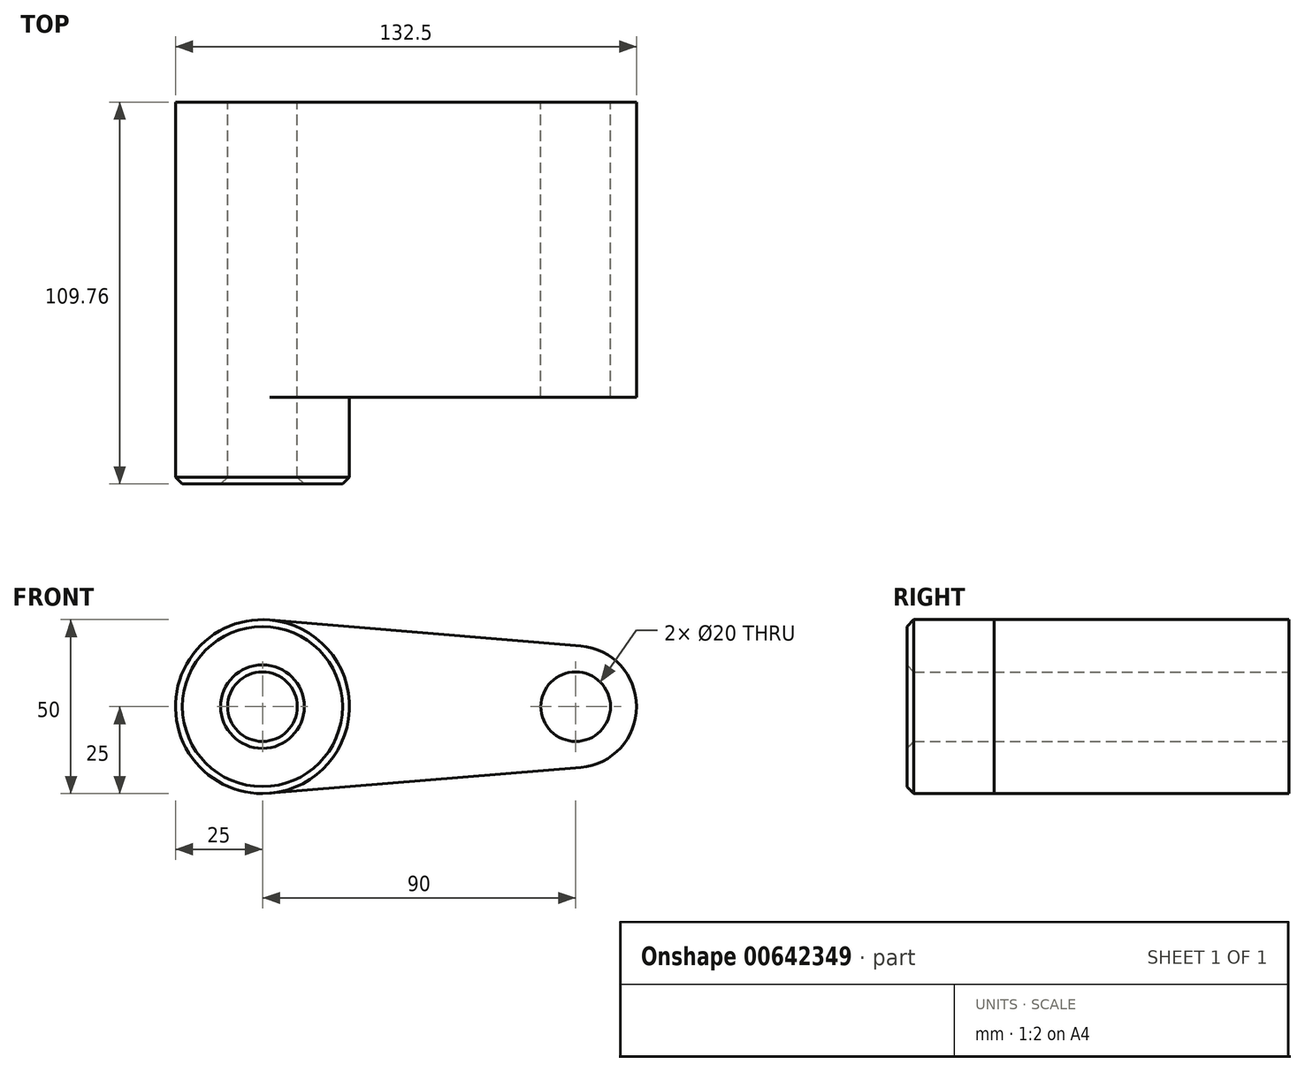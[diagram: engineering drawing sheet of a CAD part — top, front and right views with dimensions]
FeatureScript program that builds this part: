
annotation { "Feature Type Name" : "Feature", "Feature Type Description" : "" }
export const myFeature = defineFeature(function(context is Context, id is Id, definition is map)
    precondition{}
    {
        {
            var Q0;
            Q0=qCreatedBy(makeId("Front.planeOp"),FACE);
            var sketch = newSketch(context, id + "F0", { "sketchPlane" : qUnion([Q0])});
            skCircle(sketch, "E0", {"center": v(0, 0) * mm, "radius": 25 * mm});
            skCircle(sketch, "E1", {"center": v(90, 0) * mm, "radius": 17.5 * mm});
            skLineSegment(sketch, "E2", {"start": v(2.08, 24.91) * mm, "end": v(91.46, 17.44) * mm});
            skLineSegment(sketch, "E3", {"start": v(2.08, -24.91) * mm, "end": v(91.46, -17.44) * mm});
            skCircle(sketch, "E4", {"center": v(0, 0) * mm, "radius": 10 * mm});
            skCircle(sketch, "E5", {"center": v(90, 0) * mm, "radius": 10 * mm});
            skSolve(sketch);
        }
        {
            var Q0;
            Q0=qSketchRegion(id+"F0",true);
            extrude(context, id + "F1", {"entities" : qUnion([Q0]), "depth" : 25 * mm});
        }
        {
            var Q0;
            Q0=makeQuery(id+"F0.imprint","IMPRINT",FACE,{"disambiguationData":[TD([[makeQuery(id+"F0.imprint","IMPRINT",EDGE,{"derivedFrom":sQuery(id+"F0.wireOp",EDGE,"E4")}),-1.0]])]});
            extrude(context, id + "F2", {"entities" : qUnion([Q0]), "operationType" : NewBodyOperationType.ADD, "depth" : 50 * mm});
        }
        {
            var Q0;
            Q0=makeQuery(id+"F2.opExtrude","CAP_EDGE",EDGE,{"disambiguationData":[OSD([sQuery(id+"F0.wireOp",EDGE,"E0")])],"isStart":false});
            var Q1;
            Q1=makeQuery(id+"F2.opExtrude","CAP_EDGE",EDGE,{"disambiguationData":[OSD([sQuery(id+"F0.wireOp",EDGE,"E4")])],"isStart":false});
            var Q2;
            Q2=makeQuery(id+"F1.opExtrude","CAP_EDGE",EDGE,{"disambiguationData":[OSD([sQuery(id+"F0.wireOp",EDGE,"E5")])],"isStart":false});
            chamfer(context, id + "F3", {"entities" : qUnion([Q0, Q1, Q2]), "width" : 2 * mm, "tangentPropagation" : true});
        }
        {
            var Q0;
            Q0=sQuery(id+"F0.wireOp",EDGE,"E0");
            extrude(context, id + "F4", {"bodyType" : ToolBodyType.SURFACE, "surfaceEntities" : qUnion([Q0]), "depth" : 25 * mm, "offsetDistance" : 25 * mm, "hasSecondDirection" : true, "secondDirectionOppositeDirection" : true, "secondDirectionDepth" : 101.16 * mm});
        }
        {
            var Q0;
            Q0 = qSketchRegion(id + "F0", true);
            var Q1;
            Q1=makeQuery(id+"F0.imprint","IMPRINT",FACE,{"disambiguationData":[TD([[makeQuery(id+"F0.imprint","IMPRINT",EDGE,{"derivedFrom":sQuery(id+"F0.wireOp",EDGE,"E4")}),-1.0]])]});
            extrude(context, id + "F5", {"entities" : qUnion([Q0, Q1]), "operationType" : NewBodyOperationType.ADD, "depth" : 25 * mm, "offsetDistance" : 25 * mm, "hasSecondDirection" : true, "secondDirectionOppositeDirection" : true, "secondDirectionDepth" : 59.76 * mm});
        }
    });
